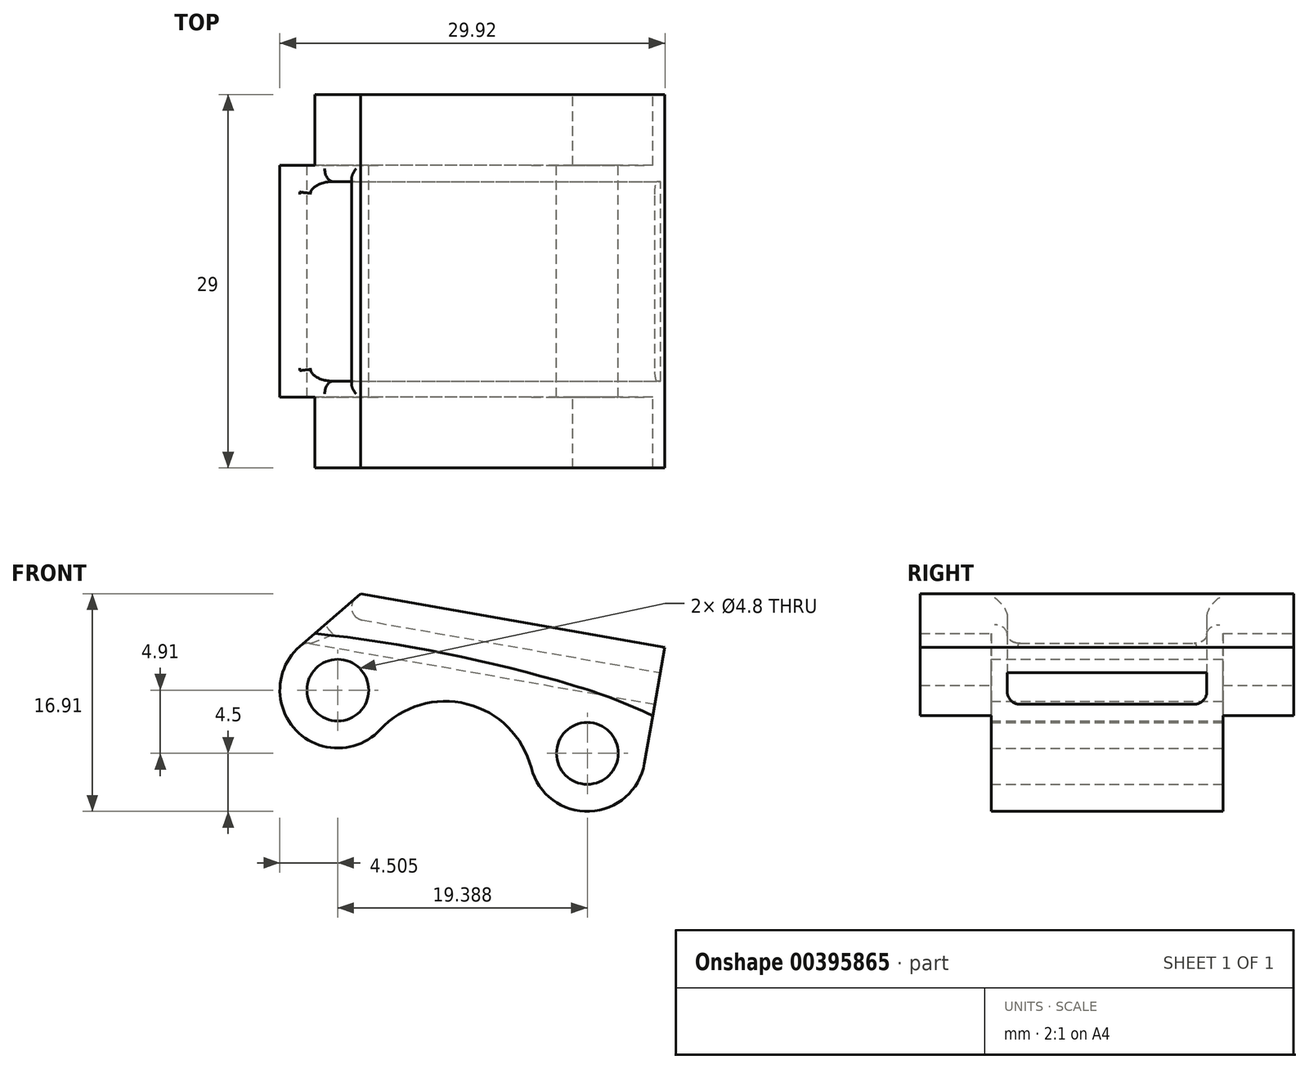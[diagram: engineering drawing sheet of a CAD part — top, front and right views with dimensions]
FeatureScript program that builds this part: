
annotation { "Feature Type Name" : "Feature", "Feature Type Description" : "" }
export const myFeature = defineFeature(function(context is Context, id is Id, definition is map)
    precondition{}
    {
        {
            var Q0;
            Q0=qCreatedBy(makeId("Front.planeOp"),FACE);
            var sketch = newSketch(context, id + "F0", { "sketchPlane" : qUnion([Q0])});
            skCircle(sketch, "E0", {"center": v(-8.96, -19.44) * mm, "radius": 2.4 * mm});
            skCircle(sketch, "E1", {"center": v(10.43, -24.35) * mm, "radius": 2.4 * mm});
            skLineSegment(sketch, "E2", {"start": v(-8.96, -19.44) * mm, "end": v(10.43, -24.35) * mm, "construction": true});
            skArc(sketch, "E3", {"start": v(-11.9, -16.04) * mm, "mid": v(-12.2, -22.57) * mm, "end": v(-5.66, -22.5) * mm});
            skArc(sketch, "E4", {"start": v(6.08, -25.48) * mm, "mid": v(10.6, -28.85) * mm, "end": v(14.86, -25.13) * mm});
            skArc(sketch, "E5", {"start": v(6.08, -25.48) * mm, "mid": v(1.09, -20.51) * mm, "end": v(-5.66, -22.5) * mm});
            skArc(sketch, "E6", {"start": v(9.31, -19.06) * mm, "mid": v(-0.62, -16.58) * mm, "end": v(-10.75, -15.04) * mm});
            skPoint(sketch, "E7.center.orphan", {"position": v(-3.72, -31.83) * mm});
            skArc(sketch, "E8", {"start": v(15.52, -21.43) * mm, "mid": v(12.46, -20.12) * mm, "end": v(9.31, -19.06) * mm});
            skLineSegment(sketch, "E9", {"start": v(16.1, -18.18) * mm, "end": v(-9.22, -13.71) * mm, "construction": true});
            skLineSegment(sketch, "E10", {"start": v(-7.18, -11.94) * mm, "end": v(16.46, -16.1) * mm});
            skLineSegment(sketch, "E11", {"start": v(16.46, -16.1) * mm, "end": v(14.86, -25.13) * mm});
            skLineSegment(sketch, "E12", {"start": v(-7.18, -11.94) * mm, "end": v(-11.9, -16.04) * mm});
            skPoint(sketch, "E13.orphan", {"position": v(16.28, -21.8) * mm});
            skSolve(sketch);
        }
        {
            var Q0;
            Q0=qSketchRegion(id+"F0",true);
            extrude(context, id + "F1", {"entities" : qUnion([Q0]), "endBound" : BoundingType.SYMMETRIC, "depth" : 18 * mm});
        }
        {
            var Q0;
            {var subQ3=sQuery(id+"F0.wireOp",EDGE,"E6");Q0=makeQuery(id+"F0.imprint","IMPRINT",FACE,{"disambiguationData":[TD([[makeQuery(id+"F0.imprint","IMPRINT",EDGE,{"derivedFrom":subQ3}),-1.0]])]});}
            extrude(context, id + "F2", {"entities" : qUnion([Q0]), "operationType" : NewBodyOperationType.ADD, "endBound" : BoundingType.SYMMETRIC, "depth" : 29 * mm});
        }
        {
            var Q0;
            {var subQ0=sQuery(id+"F0.wireOp",EDGE,"E11");Q0=makeQuery(id+"F2.boolean.opBoolean","MERGE",FACE,{"derivedFrom":[makeQuery(id+"F1.opExtrude","SWEPT_FACE",FACE,{"disambiguationData":[OSD([subQ0])]}),makeQuery(id+"F2.opExtrude","SWEPT_FACE",FACE,{"disambiguationData":[OSD([subQ0])]})]});}
            var sketch = newSketch(context, id + "F3", { "sketchPlane" : qUnion([Q0])});
            skLineSegment(sketch, "E14.bottom", {"start": v(-7.75, -15) * mm, "end": v(7.75, -15) * mm});
            skLineSegment(sketch, "E14.top", {"start": v(-6.75, -17.5) * mm, "end": v(6.75, -17.5) * mm});
            skLineSegment(sketch, "E14.left", {"start": v(-7.75, -15) * mm, "end": v(-7.75, -16.5) * mm});
            skLineSegment(sketch, "E14.right", {"start": v(7.75, -15) * mm, "end": v(7.75, -16.5) * mm});
            skPoint(sketch, "E15.visualSharp", {"position": v(-7.75, -17.5) * mm});
            skArc(sketch, "E15.filletArc", {"start": v(-7.75, -16.5) * mm, "mid": v(-7.46, -17.21) * mm, "end": v(-6.75, -17.5) * mm});
            skPoint(sketch, "E16.visualSharp", {"position": v(7.75, -17.5) * mm});
            skArc(sketch, "E16.filletArc", {"start": v(6.75, -17.5) * mm, "mid": v(7.46, -17.21) * mm, "end": v(7.75, -16.5) * mm});
            skSolve(sketch);
        }
        {
            var Q0;
            Q0 = qSketchRegion(id + "F3", true);
            extrude(context, id + "F4", {"entities" : qUnion([Q0]), "operationType" : NewBodyOperationType.REMOVE, "oppositeDirection" : true, "depth" : 40 * mm});
        }
        {
            var Q0;
            {var subQ0=sQuery(id+"F0.wireOp",EDGE,"E12");Q0=makeQuery(id+"F4.boolean.opBoolean","INTERSECT",EDGE,{"derivedFrom":[makeQuery(id+"F2.boolean.opBoolean","MERGE",FACE,{"derivedFrom":[makeQuery(id+"F1.opExtrude","SWEPT_FACE",FACE,{"disambiguationData":[OSD([subQ0])]}),makeQuery(id+"F2.opExtrude","SWEPT_FACE",FACE,{"disambiguationData":[OSD([subQ0])]})]}),makeQuery(id+"F4.opExtrude","SWEPT_FACE",FACE,{"disambiguationData":[OSD([sQuery(id+"F3.wireOp",EDGE,"E14.bottom")])]})]});}
            var Q1;
            Q1=makeQuery(id+"F4.boolean.opBoolean","COPY",EDGE,{"derivedFrom":makeQuery(id+"F4.opExtrude","CAP_EDGE",EDGE,{"disambiguationData":[OSD([sQuery(id+"F3.wireOp",EDGE,"E14.bottom")])],"isStart":true})});
            fillet(context, id + "F5", {"entities" : qUnion([Q0, Q1]), "radius" : 1 * mm, "tangentPropagation" : true, "allowEdgeOverflow" : false});
        }
        {
            var Q0;
            Q0=makeQuery(id+"F4.boolean.opBoolean","COPY",EDGE,{"derivedFrom":makeQuery(id+"F4.opExtrude","CAP_EDGE",EDGE,{"disambiguationData":[OSD([sQuery(id+"F3.wireOp",EDGE,"E14.left")])],"isStart":true})});
            var Q1;
            {var subQ0=sQuery(id+"F0.wireOp",EDGE,"E12");Q1=makeQuery(id+"F4.boolean.opBoolean","INTERSECT",EDGE,{"derivedFrom":[makeQuery(id+"F2.boolean.opBoolean","MERGE",FACE,{"derivedFrom":[makeQuery(id+"F1.opExtrude","SWEPT_FACE",FACE,{"disambiguationData":[OSD([subQ0])]}),makeQuery(id+"F2.opExtrude","SWEPT_FACE",FACE,{"disambiguationData":[OSD([subQ0])]})]}),makeQuery(id+"F4.opExtrude","SWEPT_FACE",FACE,{"disambiguationData":[OSD([sQuery(id+"F3.wireOp",EDGE,"E14.right")])]})]});}
            fillet(context, id + "F6", {"entities" : qUnion([Q0, Q1]), "radius" : 1 * mm, "tangentPropagation" : true, "allowEdgeOverflow" : false});
        }
    });
